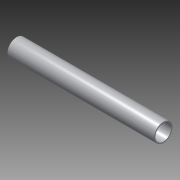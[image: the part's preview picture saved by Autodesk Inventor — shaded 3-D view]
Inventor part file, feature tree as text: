
AUTODESK INVENTOR PART (.ipt)
format: ipt  version: 2014 (Build 180170000, 170)  size: 87,552 bytes
history: native  units: in
note: dims shown in document units (in); Inventor stores cm internally (conversion verified against a paired STEP export)
features: extrude x1, sketch x1
ambient origin geometry x8: Origin, YZ Plane, XZ Plane, XY Plane, X Axis, Y Axis, Z Axis, Center Point
bodies: Solid1 (feature_tree)
feature tree (2):
  extrude  "Extrusion1"  Depth=4.0in
  sketch  "Sketch1"  dims[d0=0.5in d1=0.4375in d2=4.0in d3=0.0in]
